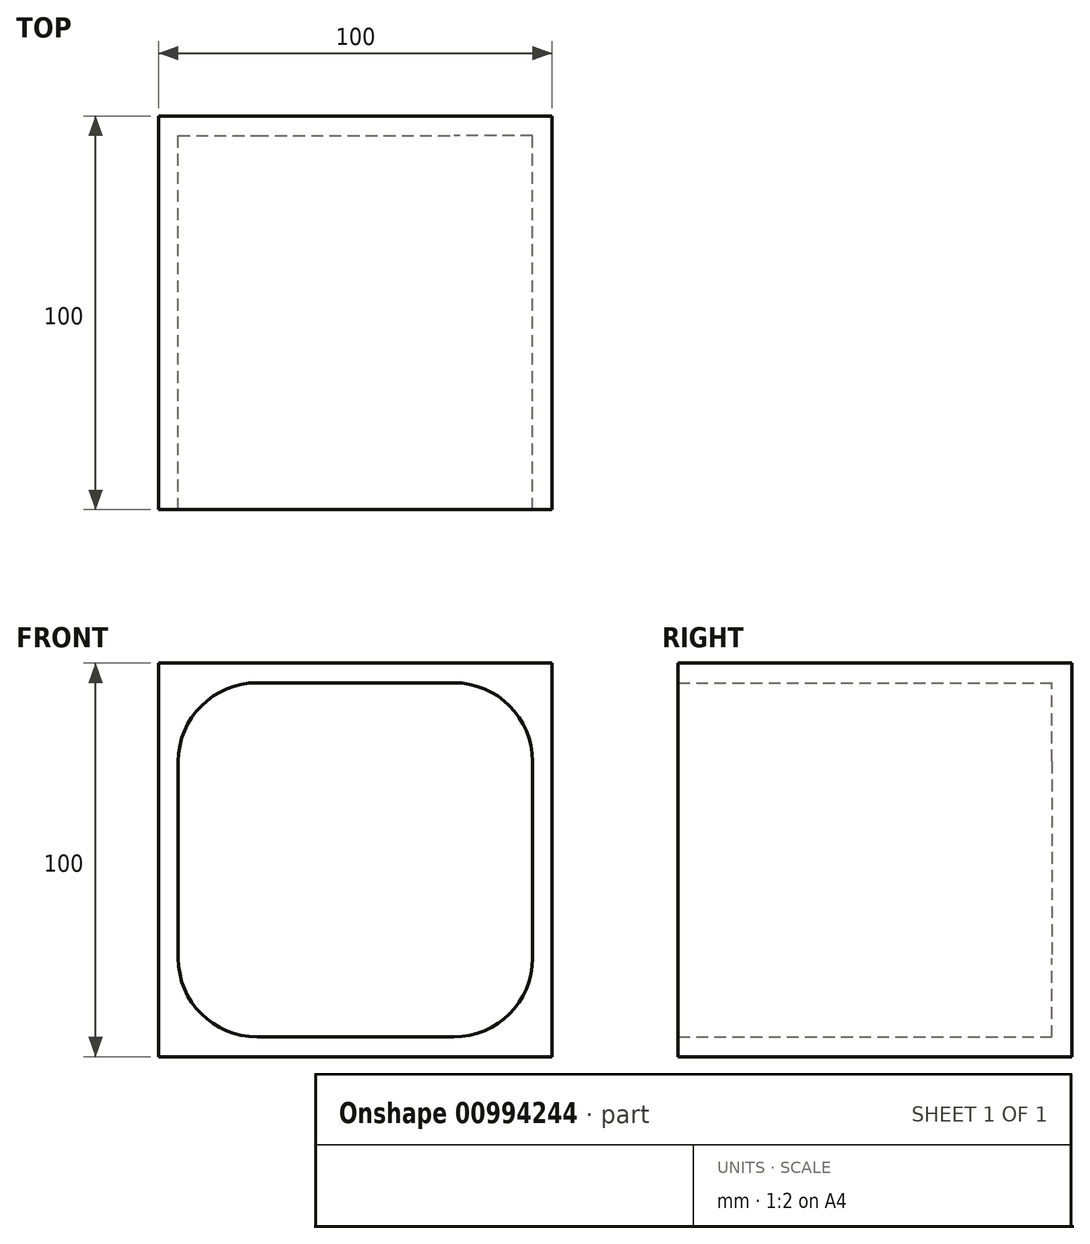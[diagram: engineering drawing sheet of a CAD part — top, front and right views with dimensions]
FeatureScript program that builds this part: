
annotation { "Feature Type Name" : "Feature", "Feature Type Description" : "" }
export const myFeature = defineFeature(function(context is Context, id is Id, definition is map)
    precondition{}
    {
        {
            var Q0;
            Q0=qCreatedBy(makeId("Top.planeOp"),FACE);
            var sketch = newSketch(context, id + "F0", { "sketchPlane" : qUnion([Q0])});
            skLineSegment(sketch, "E0.bottom", {"start": v(0, 0) * mm, "end": v(100, 0) * mm});
            skLineSegment(sketch, "E0.top", {"start": v(0, 100) * mm, "end": v(100, 100) * mm});
            skLineSegment(sketch, "E0.left", {"start": v(0, 0) * mm, "end": v(0, 100) * mm});
            skLineSegment(sketch, "E0.right", {"start": v(100, 0) * mm, "end": v(100, 100) * mm});
            skSolve(sketch);
        }
        {
            var Q0;
            Q0=makeQuery(id+"F0.imprint","IMPRINT",FACE,{"disambiguationData":[TD([[makeQuery(id+"F0.imprint","IMPRINT",EDGE,{"derivedFrom":sQuery(id+"F0.wireOp",EDGE,"E0.bottom")}),1.0]])]});
            extrude(context, id + "F1", {"entities" : qUnion([Q0]), "depth" : 100 * mm, "offsetDistance" : 25 * mm});
        }
        {
            var Q0;
            Q0=makeQuery(id+"F1.opExtrude","SWEPT_FACE",FACE,{"disambiguationData":[OSD([sQuery(id+"F0.wireOp",EDGE,"E0.bottom")])]});
            shell(context, id + "F2", {"entities" : qUnion([Q0]), "thickness" : 5 * mm});
        }
        {
            var Q0;
            {var subQ0=sQuery(id+"F0.wireOp",EDGE,"E0.right");Q0=makeQuery(id+"F2.opShell","OFFSET_EDGE",EDGE,{"disambiguationData":[OSD([subQ0]),TDD([makeQuery(id+"F1.opExtrude","CAP_EDGE",EDGE,{"disambiguationData":[OSD([subQ0])],"isStart":false})])]});}
            var Q1;
            {var subQ0=sQuery(id+"F0.wireOp",EDGE,"E0.right");Q1=makeQuery(id+"F2.opShell","OFFSET_EDGE",EDGE,{"disambiguationData":[OSD([subQ0]),TDD([makeQuery(id+"F1.opExtrude","CAP_EDGE",EDGE,{"disambiguationData":[OSD([subQ0])],"isStart":true})])]});}
            var Q2;
            {var subQ0=sQuery(id+"F0.wireOp",EDGE,"E0.left");Q2=makeQuery(id+"F2.opShell","OFFSET_EDGE",EDGE,{"disambiguationData":[OSD([subQ0]),TDD([makeQuery(id+"F1.opExtrude","CAP_EDGE",EDGE,{"disambiguationData":[OSD([subQ0])],"isStart":true})])]});}
            var Q3;
            {var subQ0=sQuery(id+"F0.wireOp",EDGE,"E0.left");Q3=makeQuery(id+"F2.opShell","OFFSET_EDGE",EDGE,{"disambiguationData":[OSD([subQ0]),TDD([makeQuery(id+"F1.opExtrude","CAP_EDGE",EDGE,{"disambiguationData":[OSD([subQ0])],"isStart":false})])]});}
            fillet(context, id + "F3", {"entities" : qUnion([Q0, Q1, Q2, Q3]), "radius" : 20 * mm, "tangentPropagation" : true, "allowEdgeOverflow" : false});
        }
    });
